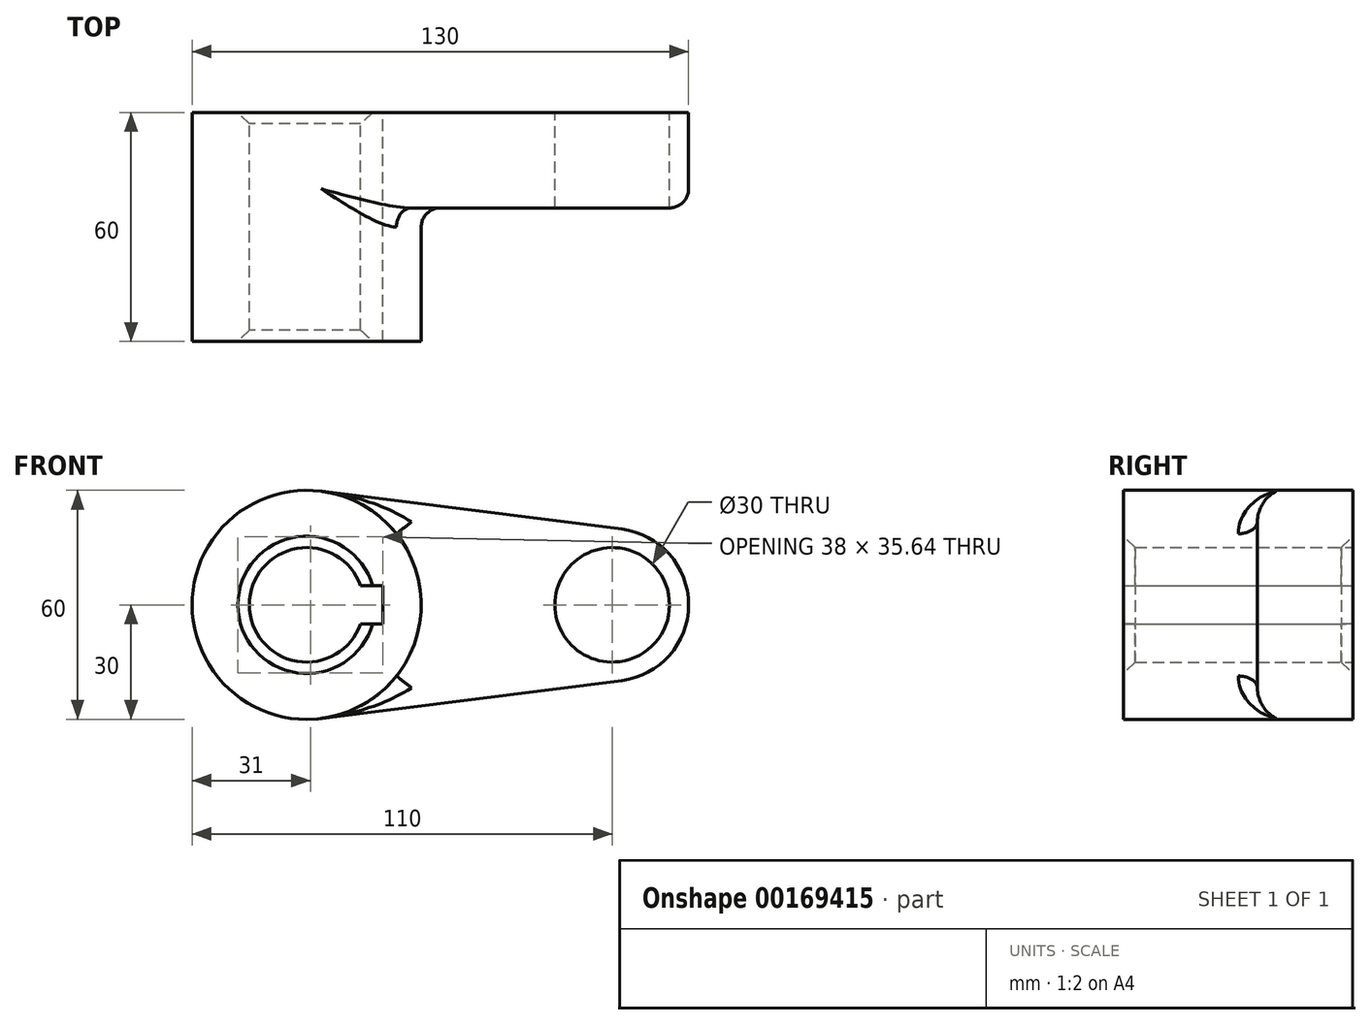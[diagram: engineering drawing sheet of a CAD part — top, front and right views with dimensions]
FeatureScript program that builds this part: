
annotation { "Feature Type Name" : "Feature", "Feature Type Description" : "" }
export const myFeature = defineFeature(function(context is Context, id is Id, definition is map)
    precondition{}
    {
        {
            var Q0;
            Q0=qCreatedBy(makeId("Front.planeOp"),FACE);
            var sketch = newSketch(context, id + "F0", { "sketchPlane" : qUnion([Q0])});
            skCircle(sketch, "E0", {"center": v(0, 0) * mm, "radius": 30 * mm});
            skCircle(sketch, "E1", {"center": v(80, 0) * mm, "radius": 20 * mm});
            skLineSegment(sketch, "E2", {"start": v(3.75, 29.76) * mm, "end": v(82.5, 19.84) * mm});
            skLineSegment(sketch, "E3", {"start": v(3.75, -29.76) * mm, "end": v(82.5, -19.84) * mm});
            skCircle(sketch, "E4", {"center": v(0, 0) * mm, "radius": 15 * mm});
            skCircle(sketch, "E5", {"center": v(80, 0) * mm, "radius": 15 * mm});
            skLineSegment(sketch, "E6.bottom", {"start": v(20, -5) * mm, "end": v(-20, -5) * mm});
            skLineSegment(sketch, "E6.top", {"start": v(20, 5) * mm, "end": v(-20, 5) * mm});
            skLineSegment(sketch, "E6.left", {"start": v(20, -5) * mm, "end": v(20, 5) * mm});
            skLineSegment(sketch, "E6.right", {"start": v(-20, -5) * mm, "end": v(-20, 5) * mm});
            skSolve(sketch);
        }
        {
            var Q0;
            {var subQ0=sQuery(id+"F0.wireOp",EDGE,"E2");Q0=makeQuery(id+"F0.imprint","IMPRINT",FACE,{"disambiguationData":[TD([[makeQuery(id+"F0.imprint","IMPRINT",EDGE,{"derivedFrom":subQ0}),-1.0]])]});}
            var Q1;
            Q1=makeQuery(id+"F0.imprint","IMPRINT",FACE,{"disambiguationData":[TD([[makeQuery(id+"F0.imprint","IMPRINT",EDGE,{"derivedFrom":sQuery(id+"F0.wireOp",EDGE,"E5")}),-1.0]])]});
            var Q2;
            {var subQ5=sQuery(id+"F0.wireOp",EDGE,"E6.right");Q2=makeQuery(id+"F0.imprint","IMPRINT",FACE,{"disambiguationData":[TD([[makeQuery(id+"F0.imprint","IMPRINT",EDGE,{"derivedFrom":subQ5}),-1.0]])]});}
            var Q3;
            {var subQ11=sQuery(id+"F0.wireOp",EDGE,"E6.left");Q3=makeQuery(id+"F0.imprint","IMPRINT",FACE,{"disambiguationData":[TD([[makeQuery(id+"F0.imprint","IMPRINT",EDGE,{"derivedFrom":subQ11}),-1.0]])]});}
            extrude(context, id + "F1", {"entities" : qUnion([Q0, Q1, Q2, Q3]), "depth" : 25 * mm});
        }
        {
            var Q0;
            {var subQ11=sQuery(id+"F0.wireOp",EDGE,"E6.left");Q0=makeQuery(id+"F0.imprint","IMPRINT",FACE,{"disambiguationData":[TD([[makeQuery(id+"F0.imprint","IMPRINT",EDGE,{"derivedFrom":subQ11}),-1.0]])]});}
            var Q1;
            {var subQ5=sQuery(id+"F0.wireOp",EDGE,"E6.right");Q1=makeQuery(id+"F0.imprint","IMPRINT",FACE,{"disambiguationData":[TD([[makeQuery(id+"F0.imprint","IMPRINT",EDGE,{"derivedFrom":subQ5}),-1.0]])]});}
            extrude(context, id + "F2", {"entities" : qUnion([Q0, Q1]), "operationType" : NewBodyOperationType.ADD, "depth" : 60 * mm});
        }
        {
            var Q0;
            {var subQ0=sQuery(id+"F0.wireOp",EDGE,"E0");Q0=makeQuery(id+"F2.boolean.opBoolean","INTERSECT",EDGE,{"derivedFrom":[makeQuery(id+"F1.opExtrude","CAP_FACE",FACE,{"disambiguationData":[OSD([subQ0,sQuery(id+"F0.wireOp",EDGE,"E1"),sQuery(id+"F0.wireOp",EDGE,"E2"),sQuery(id+"F0.wireOp",EDGE,"E3"),sQuery(id+"F0.wireOp",EDGE,"E4"),sQuery(id+"F0.wireOp",EDGE,"E5"),sQuery(id+"F0.wireOp",EDGE,"E6.bottom"),sQuery(id+"F0.wireOp",EDGE,"E6.top"),sQuery(id+"F0.wireOp",EDGE,"E6.left")])],"isStart":false}),makeQuery(id+"F2.opExtrude","SWEPT_FACE",FACE,{"disambiguationData":[OSD([subQ0])]})]});}
            var Q1;
            Q1=makeQuery(id+"F1.opExtrude","CAP_EDGE",EDGE,{"disambiguationData":[OSD([sQuery(id+"F0.wireOp",EDGE,"E3")])],"isStart":false});
            fillet(context, id + "F3", {"entities" : qUnion([Q0, Q1]), "radius" : 5 * mm, "tangentPropagation" : true, "allowEdgeOverflow" : false});
        }
        {
            var Q0;
            Q0=makeQuery(id+"F2.opExtrude","CAP_EDGE",EDGE,{"disambiguationData":[OSD([sQuery(id+"F0.wireOp",EDGE,"E4")])],"isStart":false});
            var Q1;
            Q1=makeQuery(id+"F1.opExtrude","CAP_EDGE",EDGE,{"disambiguationData":[OSD([sQuery(id+"F0.wireOp",EDGE,"E4")])],"isStart":true});
            chamfer(context, id + "F4", {"entities" : qUnion([Q0, Q1]), "width" : 3 * mm, "tangentPropagation" : true});
        }
    });
